# Revit family: Haworth_GingerAle_Chair
name_source: partatom
category: Furniture
revit_build: Autodesk Revit 2018 (Build: 20170223_1515(x64)
units: mm (PartAtom-declared; Revit-internal decimal feet)

## family parameters
Always vertical = Yes
Cut with Voids When Loaded = No
OmniClass Number = 23.40.20.00
OmniClass Title = General Furniture and Specialties
Room Calculation Point = No
Shared = No
Work Plane-Based = No

## types (5) — shared parameters
Actual Depth = 1' - 9 3/4"
Actual Height = 2' - 7"
Actual Width = 2' - 1"
Assembly Code = E2020200
Glide Finish = Haworth _ Polymer _ Slate
Hardware Finish = Haworth _ Metal _ Chrome
Manufacturer = Haworth
Model = HCPF-GA
Size = Verify Final Dim. w/ Haworth
URL = http://www.haworth.com
URL - Product = http://www.haworth.com
Version = 4
Warranty = http://www.haworth.com

## per-type parameters (varying)
| type | Column Base | Description | Five Caster Adjustable Height Base | Five Caster Fixed Height Base | Four Angled Legs | Four Legs |
| HCPF-GA - Four Legs | No | Haworth Ginger Ale Chair - Four Legs | No | No | No | Yes |
| HCPF-GA - Four Angled Legs | No | Haworth Ginger Ale Chair - Four Angled Legs | No | No | Yes | No |
| HCPF-GA - Five Caster Fixed Height Base | No | Haworth Ginger Ale Chair - Five Caster Fixed Height Base | No | Yes | No | No |
| HCPF-GA - Five Caster Adjustable Height Base | No | Haworth Ginger Ale Chair - Five Caster Adjustable Height Base | Yes | No | No | No |
| HCPF-GA - Column Base | Yes | Haworth Ginger Ale Chair - Column Base | No | No | No | No |

## geometry (parser evidence)
native form markers: Sweep x5
no freeform markers — native parametric forms only
